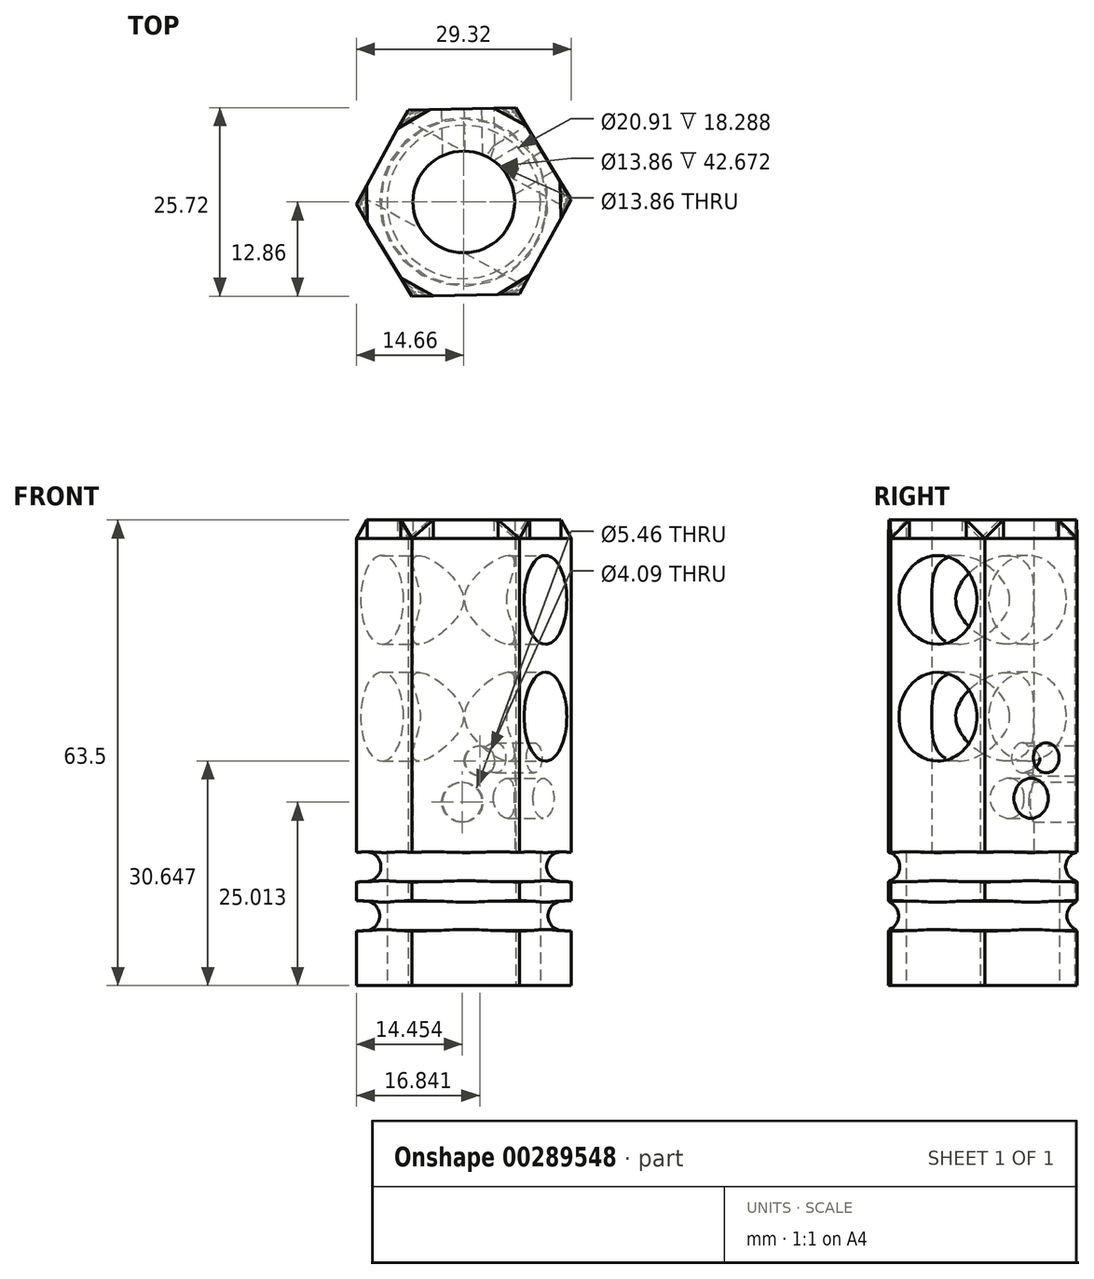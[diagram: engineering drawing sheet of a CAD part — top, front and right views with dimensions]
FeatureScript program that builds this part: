
annotation { "Feature Type Name" : "Feature", "Feature Type Description" : "" }
export const myFeature = defineFeature(function(context is Context, id is Id, definition is map)
    precondition{}
    {
        {
            var Q0;
            Q0=qCreatedBy(makeId("Top.planeOp"),FACE);
            var sketch = newSketch(context, id + "F0", { "sketchPlane" : qUnion([Q0])});
            skCircle(sketch, "E0.cCircle", {"center": v(0, 0) * mm, "radius": 12.7 * mm, "construction": true});
            skLineSegment(sketch, "E0.0", {"start": v(14.66, 0.32) * mm, "end": v(7.6, -12.54) * mm});
            skLineSegment(sketch, "E0.1", {"start": v(7.6, -12.54) * mm, "end": v(-7.06, -12.86) * mm});
            skLineSegment(sketch, "E0.2", {"start": v(-7.06, -12.86) * mm, "end": v(-14.66, -0.32) * mm});
            skLineSegment(sketch, "E0.3", {"start": v(-14.66, -0.32) * mm, "end": v(-7.6, 12.54) * mm});
            skLineSegment(sketch, "E0.4", {"start": v(-7.6, 12.54) * mm, "end": v(7.06, 12.86) * mm});
            skLineSegment(sketch, "E0.5", {"start": v(7.06, 12.86) * mm, "end": v(14.66, 0.32) * mm});
            skPoint(sketch, "E0.0.midPoint", {"position": v(11.13, -6.11) * mm});
            skSolve(sketch);
        }
        {
            var Q0;
            Q0=makeQuery(id+"F0.imprint","IMPRINT",FACE,{"disambiguationData":[TD([[makeQuery(id+"F0.imprint","IMPRINT",EDGE,{"derivedFrom":sQuery(id+"F0.wireOp",EDGE,"E0.0")}),-1.0]])]});
            extrude(context, id + "F1", {"entities" : qUnion([Q0]), "depth" : 60.96 * mm});
        }
        {
            var Q0;
            Q0=makeQuery(id+"F1.opExtrude","CAP_FACE",FACE,{"disambiguationData":[OSD([sQuery(id+"F0.wireOp",EDGE,"E0.0"),sQuery(id+"F0.wireOp",EDGE,"E0.1"),sQuery(id+"F0.wireOp",EDGE,"E0.2"),sQuery(id+"F0.wireOp",EDGE,"E0.3"),sQuery(id+"F0.wireOp",EDGE,"E0.4"),sQuery(id+"F0.wireOp",EDGE,"E0.5")])],"isStart":true});
            var sketch = newSketch(context, id + "F2", { "sketchPlane" : qUnion([Q0])});
            skCircle(sketch, "E1", {"center": v(0, 0) * mm, "radius": 10.45 * mm});
            skSolve(sketch);
        }
        {
            var Q0;
            Q0 = qSketchRegion(id + "F2", true);
            extrude(context, id + "F3", {"entities" : qUnion([Q0]), "operationType" : NewBodyOperationType.REMOVE, "oppositeDirection" : true, "depth" : 18.29 * mm});
        }
        {
            var Q0;
            Q0=makeQuery(id+"F3.boolean.opBoolean","COPY",FACE,{"derivedFrom":makeQuery(id+"F3.opExtrude","CAP_FACE",FACE,{"disambiguationData":[OSD([sQuery(id+"F2.wireOp",EDGE,"E1")])],"isStart":false})});
            var sketch = newSketch(context, id + "F4", { "sketchPlane" : qUnion([Q0])});
            skCircle(sketch, "E2", {"center": v(0, 0) * mm, "radius": 6.93 * mm});
            skSolve(sketch);
        }
        {
            var Q0;
            Q0 = qSketchRegion(id + "F4", true);
            extrude(context, id + "F5", {"entities" : qUnion([Q0]), "operationType" : NewBodyOperationType.REMOVE, "oppositeDirection" : true, "depth" : 55.63 * mm});
        }
        {
            var Q0;
            Q0=makeQuery(id+"F1.opExtrude","CAP_FACE",FACE,{"disambiguationData":[OSD([sQuery(id+"F0.wireOp",EDGE,"E0.0"),sQuery(id+"F0.wireOp",EDGE,"E0.1"),sQuery(id+"F0.wireOp",EDGE,"E0.2"),sQuery(id+"F0.wireOp",EDGE,"E0.3"),sQuery(id+"F0.wireOp",EDGE,"E0.4"),sQuery(id+"F0.wireOp",EDGE,"E0.5")])],"isStart":false});
            var sketch = newSketch(context, id + "F6", { "sketchPlane" : qUnion([Q0])});
            skSolve(sketch);
        }
        {
            var Q0;
            Q0 = qSketchRegion(id + "F6", true);
            var Q1;
            {var subQ3=sQuery(id+"F0.wireOp",EDGE,"E0.0");Q1=makeQuery(id+"F6.imprint","IMPRINT",FACE,{"disambiguationData":[TD([[makeQuery(id+"F6.imprint","IMPRINT",EDGE,{"derivedFrom":makeQuery(id+"F1.opExtrude","CAP_EDGE",EDGE,{"disambiguationData":[OSD([subQ3])],"isStart":false})}),-1.0]])]});}
            extrude(context, id + "F7", {"entities" : qUnion([Q0, Q1]), "depth" : 2.54 * mm});
        }
        {
            var Q0;
            Q0=makeQuery(id+"F7.opExtrude","SWEPT_EDGE",EDGE,{"disambiguationData":[OSD([sQuery(id+"F0.wireOp",EDGE,"E0.4"),sQuery(id+"F0.wireOp",EDGE,"E0.5")])]});
            var Q1;
            Q1=makeQuery(id+"F7.opExtrude","SWEPT_EDGE",EDGE,{"disambiguationData":[OSD([sQuery(id+"F0.wireOp",EDGE,"E0.0"),sQuery(id+"F0.wireOp",EDGE,"E0.1")])]});
            var Q2;
            Q2=makeQuery(id+"F7.opExtrude","SWEPT_EDGE",EDGE,{"disambiguationData":[OSD([sQuery(id+"F0.wireOp",EDGE,"E0.1"),sQuery(id+"F0.wireOp",EDGE,"E0.2")])]});
            var Q3;
            Q3=makeQuery(id+"F7.opExtrude","SWEPT_EDGE",EDGE,{"disambiguationData":[OSD([sQuery(id+"F0.wireOp",EDGE,"E0.0"),sQuery(id+"F0.wireOp",EDGE,"E0.5")])]});
            var Q4;
            Q4=makeQuery(id+"F7.opExtrude","SWEPT_EDGE",EDGE,{"disambiguationData":[OSD([sQuery(id+"F0.wireOp",EDGE,"E0.2"),sQuery(id+"F0.wireOp",EDGE,"E0.3")])]});
            var Q5;
            Q5=makeQuery(id+"F7.opExtrude","SWEPT_EDGE",EDGE,{"disambiguationData":[OSD([sQuery(id+"F0.wireOp",EDGE,"E0.3"),sQuery(id+"F0.wireOp",EDGE,"E0.4")])]});
            chamfer(context, id + "F8", {"entities" : qUnion([Q0, Q1, Q2, Q3, Q4, Q5]), "width" : 5.08 * mm, "tangentPropagation" : true});
        }
        {
            var Q0;
            Q0=makeQuery(id+"F8.opChamfer","BLEND_FACE",FACE,{"disambiguationData":[OSD([sQuery(id+"F0.wireOp",EDGE,"E0.0"),sQuery(id+"F0.wireOp",EDGE,"E0.1")])]});
            var Q1;
            Q1=makeQuery(id+"F1.opExtrude","CAP_VERTEX",VERTEX,{"disambiguationData":[OSD([sQuery(id+"F0.wireOp",EDGE,"E0.0"),sQuery(id+"F0.wireOp",EDGE,"E0.1")])],"isStart":false});
            loft(context, id + "F9", {"sheetProfilesArray" : [{ "sheetProfileEntities" : qUnion([Q0]) }, { "sheetProfileEntities" : qUnion([Q1]) }]});
        }
        {
            var Q0;
            Q0=makeQuery(id+"F8.opChamfer","BLEND_FACE",FACE,{"disambiguationData":[OSD([sQuery(id+"F0.wireOp",EDGE,"E0.1"),sQuery(id+"F0.wireOp",EDGE,"E0.2")])]});
            var Q1;
            Q1=makeQuery(id+"F1.opExtrude","CAP_VERTEX",VERTEX,{"disambiguationData":[OSD([sQuery(id+"F0.wireOp",EDGE,"E0.1"),sQuery(id+"F0.wireOp",EDGE,"E0.2")])],"isStart":false});
            loft(context, id + "F10", {"sheetProfilesArray" : [{ "sheetProfileEntities" : qUnion([Q0]) }, { "sheetProfileEntities" : qUnion([Q1]) }]});
        }
        {
            var Q0;
            Q0=makeQuery(id+"F8.opChamfer","BLEND_FACE",FACE,{"disambiguationData":[OSD([sQuery(id+"F0.wireOp",EDGE,"E0.0"),sQuery(id+"F0.wireOp",EDGE,"E0.5")])]});
            var Q1;
            Q1=makeQuery(id+"F1.opExtrude","CAP_VERTEX",VERTEX,{"disambiguationData":[OSD([sQuery(id+"F0.wireOp",EDGE,"E0.0"),sQuery(id+"F0.wireOp",EDGE,"E0.5")])],"isStart":false});
            loft(context, id + "F11", {"sheetProfilesArray" : [{ "sheetProfileEntities" : qUnion([Q0]) }, { "sheetProfileEntities" : qUnion([Q1]) }]});
        }
        {
            var Q0;
            Q0=makeQuery(id+"F8.opChamfer","BLEND_FACE",FACE,{"disambiguationData":[OSD([sQuery(id+"F0.wireOp",EDGE,"E0.4"),sQuery(id+"F0.wireOp",EDGE,"E0.5")])]});
            var Q1;
            Q1=makeQuery(id+"F1.opExtrude","CAP_VERTEX",VERTEX,{"disambiguationData":[OSD([sQuery(id+"F0.wireOp",EDGE,"E0.4"),sQuery(id+"F0.wireOp",EDGE,"E0.5")])],"isStart":false});
            loft(context, id + "F12", {"sheetProfilesArray" : [{ "sheetProfileEntities" : qUnion([Q0]) }, { "sheetProfileEntities" : qUnion([Q1]) }]});
        }
        {
            var Q0;
            Q0=makeQuery(id+"F8.opChamfer","BLEND_FACE",FACE,{"disambiguationData":[OSD([sQuery(id+"F0.wireOp",EDGE,"E0.3"),sQuery(id+"F0.wireOp",EDGE,"E0.4")])]});
            var Q1;
            Q1=makeQuery(id+"F1.opExtrude","CAP_VERTEX",VERTEX,{"disambiguationData":[OSD([sQuery(id+"F0.wireOp",EDGE,"E0.3"),sQuery(id+"F0.wireOp",EDGE,"E0.4")])],"isStart":false});
            loft(context, id + "F13", {"sheetProfilesArray" : [{ "sheetProfileEntities" : qUnion([Q0]) }, { "sheetProfileEntities" : qUnion([Q1]) }]});
        }
        {
            var Q0;
            Q0=makeQuery(id+"F8.opChamfer","BLEND_FACE",FACE,{"disambiguationData":[OSD([sQuery(id+"F0.wireOp",EDGE,"E0.2"),sQuery(id+"F0.wireOp",EDGE,"E0.3")])]});
            var Q1;
            Q1=makeQuery(id+"F1.opExtrude","CAP_VERTEX",VERTEX,{"disambiguationData":[OSD([sQuery(id+"F0.wireOp",EDGE,"E0.2"),sQuery(id+"F0.wireOp",EDGE,"E0.3")])],"isStart":false});
            loft(context, id + "F14", {"sheetProfilesArray" : [{ "sheetProfileEntities" : qUnion([Q0]) }, { "sheetProfileEntities" : qUnion([Q1]) }]});
        }
        {
            var Q0;
            Q0=makeQuery(id+"F1.opExtrude","SWEPT_FACE",FACE,{"disambiguationData":[OSD([sQuery(id+"F0.wireOp",EDGE,"E0.0")])]});
            var sketch = newSketch(context, id + "F15", { "sketchPlane" : qUnion([Q0])});
            skCircle(sketch, "E3", {"center": v(0, 52.6) * mm, "radius": 6.05 * mm});
            skSolve(sketch);
        }
        {
            var Q0;
            Q0 = qSketchRegion(id + "F15", true);
            extrude(context, id + "F16", {"entities" : qUnion([Q0]), "operationType" : NewBodyOperationType.REMOVE, "oppositeDirection" : true, "depth" : 25.4 * mm});
        }
        {
            var Q0;
            Q0=makeQuery(id+"F1.opExtrude","SWEPT_FACE",FACE,{"disambiguationData":[OSD([sQuery(id+"F0.wireOp",EDGE,"E0.0")])]});
            var sketch = newSketch(context, id + "F17", { "sketchPlane" : qUnion([Q0])});
            skCircle(sketch, "E4", {"center": v(0, 36.66) * mm, "radius": 6.05 * mm});
            skSolve(sketch);
        }
        {
            var Q0;
            Q0 = qSketchRegion(id + "F17", true);
            extrude(context, id + "F18", {"entities" : qUnion([Q0]), "operationType" : NewBodyOperationType.REMOVE, "oppositeDirection" : true, "depth" : 25.4 * mm});
        }
        {
            var Q0;
            Q0=qCreatedBy(makeId("Right.planeOp"),FACE);
            var sketch = newSketch(context, id + "F19", { "sketchPlane" : qUnion([Q0])});
            skCircle(sketch, "E5", {"center": v(13.31, 16.2) * mm, "radius": 2.02 * mm});
            skSolve(sketch);
        }
        {
            var Q0;
            Q0=makeQuery(id+"F19.imprint","IMPRINT",FACE,{"disambiguationData":[TD([[makeQuery(id+"F19.imprint","IMPRINT",EDGE,{"derivedFrom":sQuery(id+"F19.wireOp",EDGE,"E5")}),1.0]])]});
            var Q1;
            Q1=makeQuery(id+"F7.opExtrude","CAP_EDGE",EDGE,{"disambiguationData":[OSD([sQuery(id+"F0.wireOp",EDGE,"E0.0"),sQuery(id+"F0.wireOp",EDGE,"E0.1"),sQuery(id+"F0.wireOp",EDGE,"E0.2"),sQuery(id+"F0.wireOp",EDGE,"E0.3"),sQuery(id+"F0.wireOp",EDGE,"E0.4"),sQuery(id+"F0.wireOp",EDGE,"E0.5"),sQuery(id+"F4.wireOp",EDGE,"E2")])],"isStart":false});
            revolve(context, id + "F20", {"operationType" : NewBodyOperationType.REMOVE, "entities" : qUnion([Q0]), "axis" : qUnion([Q1]), "revolveType" : RevolveType.FULL, "oppositeDirection" : true});
        }
        {
            var Q0;
            {var subQ0=sQuery(id+"F0.wireOp",EDGE,"E0.0");var subQ1=sQuery(id+"F0.wireOp",EDGE,"E0.5");var subQ2=sQuery(id+"F0.wireOp",EDGE,"E0.4");Q0=makeQuery(id+"F20.boolean.opBoolean","SPLIT",FACE,{"disambiguationData":[TD([makeQuery(id+"F1.opExtrude","CAP_FACE",FACE,{"disambiguationData":[OSD([subQ0,sQuery(id+"F0.wireOp",EDGE,"E0.1"),sQuery(id+"F0.wireOp",EDGE,"E0.2"),sQuery(id+"F0.wireOp",EDGE,"E0.3"),subQ2,subQ1])],"isStart":false})])],"derivedFrom":makeQuery(id+"F1.opExtrude","SWEPT_FACE",FACE,{"disambiguationData":[OSD([subQ1])]})});}
            var sketch = newSketch(context, id + "F21", { "sketchPlane" : qUnion([Q0])});
            skCircle(sketch, "E6", {"center": v(2.43, 31.06) * mm, "radius": 2.04 * mm});
            skCircle(sketch, "E7", {"center": v(0, 25.54) * mm, "radius": 2.73 * mm});
            skSolve(sketch);
        }
        {
            var Q0;
            {var subQ0=sQuery(id+"F0.wireOp",EDGE,"E0.5");var subQ1=sQuery(id+"F0.wireOp",EDGE,"E0.4");var subQ2=sQuery(id+"F0.wireOp",EDGE,"E0.3");Q0=makeQuery(id+"F20.boolean.opBoolean","SPLIT",FACE,{"disambiguationData":[TD([makeQuery(id+"F1.opExtrude","CAP_FACE",FACE,{"disambiguationData":[OSD([sQuery(id+"F0.wireOp",EDGE,"E0.0"),sQuery(id+"F0.wireOp",EDGE,"E0.1"),sQuery(id+"F0.wireOp",EDGE,"E0.2"),subQ2,subQ1,subQ0])],"isStart":false})])],"derivedFrom":makeQuery(id+"F1.opExtrude","SWEPT_FACE",FACE,{"disambiguationData":[OSD([subQ1])]})});}
            var sketch = newSketch(context, id + "F22", { "sketchPlane" : qUnion([Q0])});
            skCircle(sketch, "E8", {"center": v(-2.38, 30.65) * mm, "radius": 2.04 * mm});
            skCircle(sketch, "E9", {"center": v(0, 25.01) * mm, "radius": 2.73 * mm});
            skSolve(sketch);
        }
        {
            var Q0;
            Q0 = qSketchRegion(id + "F22", true);
            extrude(context, id + "F23", {"entities" : qUnion([Q0]), "operationType" : NewBodyOperationType.REMOVE, "oppositeDirection" : true, "depth" : 12.7 * mm});
        }
        {
            var Q0;
            Q0 = qSketchRegion(id + "F21", true);
            extrude(context, id + "F24", {"entities" : qUnion([Q0]), "operationType" : NewBodyOperationType.REMOVE, "oppositeDirection" : true, "depth" : 12.7 * mm});
        }
        {
            var Q0;
            Q0=qCreatedBy(makeId("Right.planeOp"),FACE);
            var sketch = newSketch(context, id + "F25", { "sketchPlane" : qUnion([Q0])});
            skCircle(sketch, "E10", {"center": v(13.68, 16.2) * mm, "radius": 2.03 * mm});
            skSolve(sketch);
        }
        {
            var Q0;
            Q0 = qSketchRegion(id + "F25", true);
            var Q1;
            Q1=makeQuery(id+"F7.opExtrude","CAP_EDGE",EDGE,{"disambiguationData":[OSD([sQuery(id+"F0.wireOp",EDGE,"E0.0"),sQuery(id+"F0.wireOp",EDGE,"E0.1"),sQuery(id+"F0.wireOp",EDGE,"E0.2"),sQuery(id+"F0.wireOp",EDGE,"E0.3"),sQuery(id+"F0.wireOp",EDGE,"E0.4"),sQuery(id+"F0.wireOp",EDGE,"E0.5"),sQuery(id+"F4.wireOp",EDGE,"E2")])],"isStart":false});
            revolve(context, id + "F26", {"operationType" : NewBodyOperationType.REMOVE, "entities" : qUnion([Q0]), "axis" : qUnion([Q1]), "revolveType" : RevolveType.FULL});
        }
        {
            var Q0;
            Q0=qCreatedBy(makeId("Right.planeOp"),FACE);
            var sketch = newSketch(context, id + "F27", { "sketchPlane" : qUnion([Q0])});
            skCircle(sketch, "E11", {"center": v(14.45, 16.16) * mm, "radius": 2.03 * mm});
            skSolve(sketch);
        }
        {
            var Q0;
            Q0=makeQuery(id+"F27.imprint","IMPRINT",FACE,{"disambiguationData":[TD([[makeQuery(id+"F27.imprint","IMPRINT",EDGE,{"derivedFrom":sQuery(id+"F27.wireOp",EDGE,"E11")}),1.0]])]});
            var Q1;
            Q1=makeQuery(id+"F7.opExtrude","CAP_EDGE",EDGE,{"disambiguationData":[OSD([sQuery(id+"F0.wireOp",EDGE,"E0.0"),sQuery(id+"F0.wireOp",EDGE,"E0.1"),sQuery(id+"F0.wireOp",EDGE,"E0.2"),sQuery(id+"F0.wireOp",EDGE,"E0.3"),sQuery(id+"F0.wireOp",EDGE,"E0.4"),sQuery(id+"F0.wireOp",EDGE,"E0.5"),sQuery(id+"F4.wireOp",EDGE,"E2")])],"isStart":false});
            revolve(context, id + "F28", {"operationType" : NewBodyOperationType.REMOVE, "entities" : qUnion([Q0]), "axis" : qUnion([Q1]), "revolveType" : RevolveType.FULL, "oppositeDirection" : true});
        }
        {
            var Q0;
            Q0=qCreatedBy(makeId("Right.planeOp"),FACE);
            var sketch = newSketch(context, id + "F29", { "sketchPlane" : qUnion([Q0])});
            skCircle(sketch, "E12", {"center": v(13.5, 9.5) * mm, "radius": 2.02 * mm});
            skCircle(sketch, "E13", {"center": v(14.24, 9.5) * mm, "radius": 2.08 * mm});
            skSolve(sketch);
        }
        {
            var Q0;
            Q0=makeQuery(id+"F29.imprint","IMPRINT",FACE,{"disambiguationData":[TD([[makeQuery(id+"F29.imprint","IMPRINT",EDGE,{"derivedFrom":sQuery(id+"F29.wireOp",EDGE,"E12")}),1.0]])]});
            var Q1;
            Q1=makeQuery(id+"F7.opExtrude","CAP_EDGE",EDGE,{"disambiguationData":[OSD([sQuery(id+"F0.wireOp",EDGE,"E0.0"),sQuery(id+"F0.wireOp",EDGE,"E0.1"),sQuery(id+"F0.wireOp",EDGE,"E0.2"),sQuery(id+"F0.wireOp",EDGE,"E0.3"),sQuery(id+"F0.wireOp",EDGE,"E0.4"),sQuery(id+"F0.wireOp",EDGE,"E0.5"),sQuery(id+"F4.wireOp",EDGE,"E2")])],"isStart":false});
            revolve(context, id + "F30", {"operationType" : NewBodyOperationType.REMOVE, "entities" : qUnion([Q0]), "axis" : qUnion([Q1]), "revolveType" : RevolveType.FULL, "oppositeDirection" : true});
        }
        {
            var Q0;
            {var subQ0=sQuery(id+"F29.wireOp",EDGE,"E13");var subQ1=sQuery(id+"F29.wireOp",EDGE,"E12");var subQ2=makeQuery(id+"F29.imprint","INTERSECT",VERTEX,{"disambiguationData":[OD(0.0)],"derivedFrom":[subQ1,subQ0]});Q0=makeQuery(id+"F29.imprint","IMPRINT",FACE,{"disambiguationData":[TD([[makeQuery(id+"F29.imprint","IMPRINT",EDGE,{"disambiguationData":[TD([[subQ2,-1.0]])],"derivedFrom":subQ1}),-1.0]])]});}
            var Q1;
            Q1=sQuery(id+"F2.wireOp",EDGE,"E1");
            revolve(context, id + "F31", {"operationType" : NewBodyOperationType.REMOVE, "entities" : qUnion([Q0]), "axis" : qUnion([Q1]), "revolveType" : RevolveType.FULL, "oppositeDirection" : true});
        }
    });
